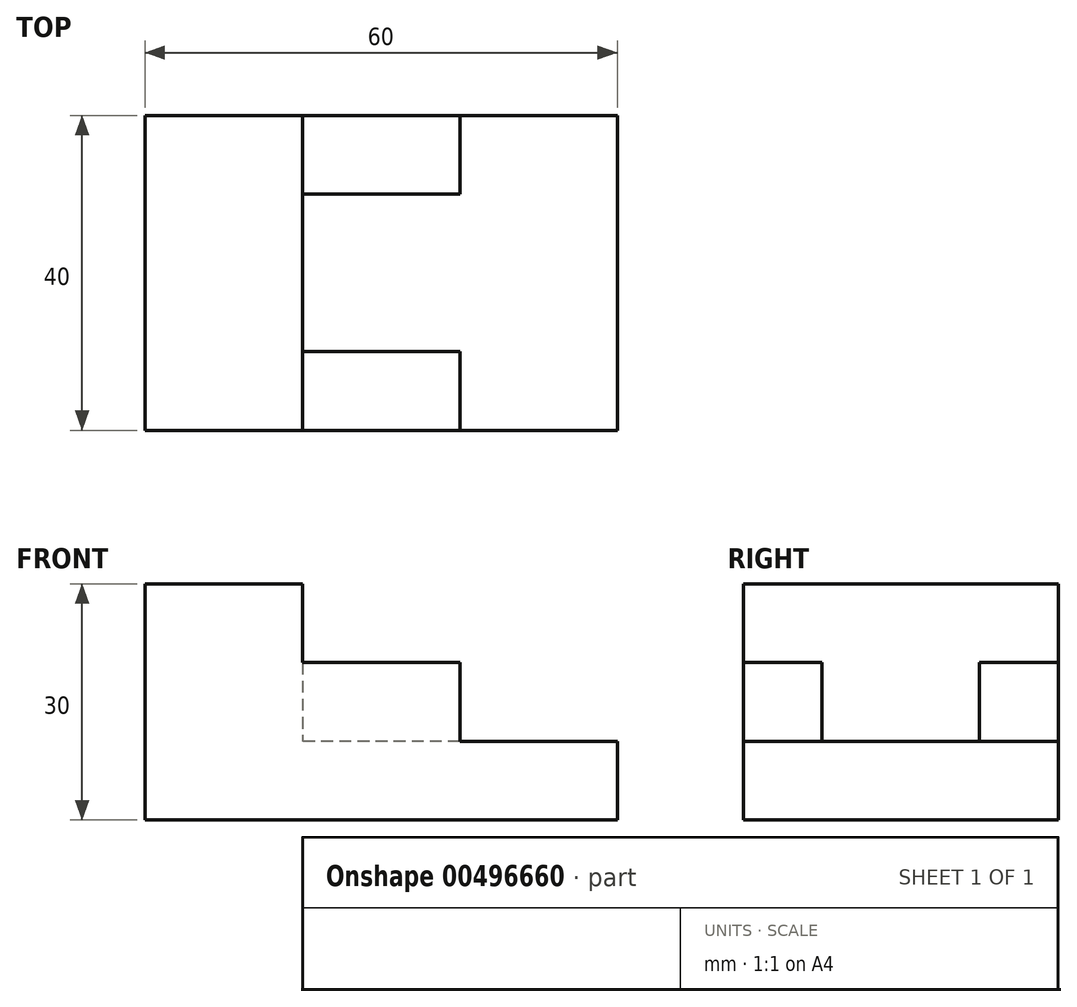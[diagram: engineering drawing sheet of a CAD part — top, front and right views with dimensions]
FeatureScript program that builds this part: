
annotation { "Feature Type Name" : "Feature", "Feature Type Description" : "" }
export const myFeature = defineFeature(function(context is Context, id is Id, definition is map)
    precondition{}
    {
        {
            var Q0;
            Q0=qCreatedBy(makeId("Top.planeOp"),FACE);
            var sketch = newSketch(context, id + "F0", { "sketchPlane" : qUnion([Q0])});
            skLineSegment(sketch, "E0", {"start": v(0, 0) * mm, "end": v(0, 40) * mm});
            skLineSegment(sketch, "E1", {"start": v(0, 40) * mm, "end": v(60, 40) * mm});
            skLineSegment(sketch, "E2", {"start": v(60, 40) * mm, "end": v(60, 0) * mm});
            skLineSegment(sketch, "E3", {"start": v(60, 0) * mm, "end": v(0, 0) * mm});
            skLineSegment(sketch, "E4", {"start": v(0, 0) * mm, "end": v(20, 0) * mm});
            skLineSegment(sketch, "E5", {"start": v(20, 0) * mm, "end": v(20, 40) * mm});
            skSolve(sketch);
        }
        {
            var Q0;
            {var subQ0=sQuery(id+"F0.wireOp",EDGE,"E0");Q0=makeQuery(id+"F0.imprint","IMPRINT",FACE,{"disambiguationData":[TD([[makeQuery(id+"F0.imprint","IMPRINT",EDGE,{"derivedFrom":subQ0}),-1.0]])]});}
            extrude(context, id + "F1", {"entities" : qUnion([Q0]), "depth" : 30 * mm});
        }
        {
            var Q0;
            {var subQ0=sQuery(id+"F0.wireOp",EDGE,"E2");Q0=makeQuery(id+"F0.imprint","IMPRINT",FACE,{"disambiguationData":[TD([[makeQuery(id+"F0.imprint","IMPRINT",EDGE,{"derivedFrom":subQ0}),-1.0]])]});}
            extrude(context, id + "F2", {"entities" : qUnion([Q0]), "operationType" : NewBodyOperationType.ADD, "depth" : 10 * mm});
        }
        {
            var Q0;
            Q0=makeQuery(id+"F2.opExtrude","CAP_FACE",FACE,{"disambiguationData":[OSD([sQuery(id+"F0.wireOp",EDGE,"E1"),sQuery(id+"F0.wireOp",EDGE,"E2"),sQuery(id+"F0.wireOp",EDGE,"E3"),sQuery(id+"F0.wireOp",EDGE,"E5")])],"isStart":false});
            var sketch = newSketch(context, id + "F3", { "sketchPlane" : qUnion([Q0])});
            skLineSegment(sketch, "E6", {"start": v(20, 0) * mm, "end": v(40, 0) * mm});
            skLineSegment(sketch, "E7", {"start": v(40, 0) * mm, "end": v(40, 10) * mm});
            skLineSegment(sketch, "E8", {"start": v(40, 10) * mm, "end": v(20, 10) * mm});
            skLineSegment(sketch, "E9", {"start": v(20, 40) * mm, "end": v(40, 40) * mm});
            skLineSegment(sketch, "E10", {"start": v(40, 40) * mm, "end": v(40, 30) * mm});
            skLineSegment(sketch, "E11", {"start": v(40, 30) * mm, "end": v(20, 30) * mm});
            skPoint(sketch, "E11.endSnap0", {"position": v(20, 20) * mm});
            skSolve(sketch);
        }
        {
            var Q0;
            {var subQ0=sQuery(id+"F3.wireOp",EDGE,"E6");Q0=makeQuery(id+"F3.imprint","IMPRINT",FACE,{"disambiguationData":[TD([[makeQuery(id+"F3.imprint","IMPRINT",EDGE,{"derivedFrom":subQ0}),-1.0]])]});}
            var Q1;
            {var subQ0=sQuery(id+"F3.wireOp",EDGE,"E9");Q1=makeQuery(id+"F3.imprint","IMPRINT",FACE,{"disambiguationData":[TD([[makeQuery(id+"F3.imprint","IMPRINT",EDGE,{"derivedFrom":subQ0}),-1.0]])]});}
            extrude(context, id + "F4", {"entities" : qUnion([Q0, Q1]), "operationType" : NewBodyOperationType.ADD, "depth" : 10 * mm});
        }
    });
